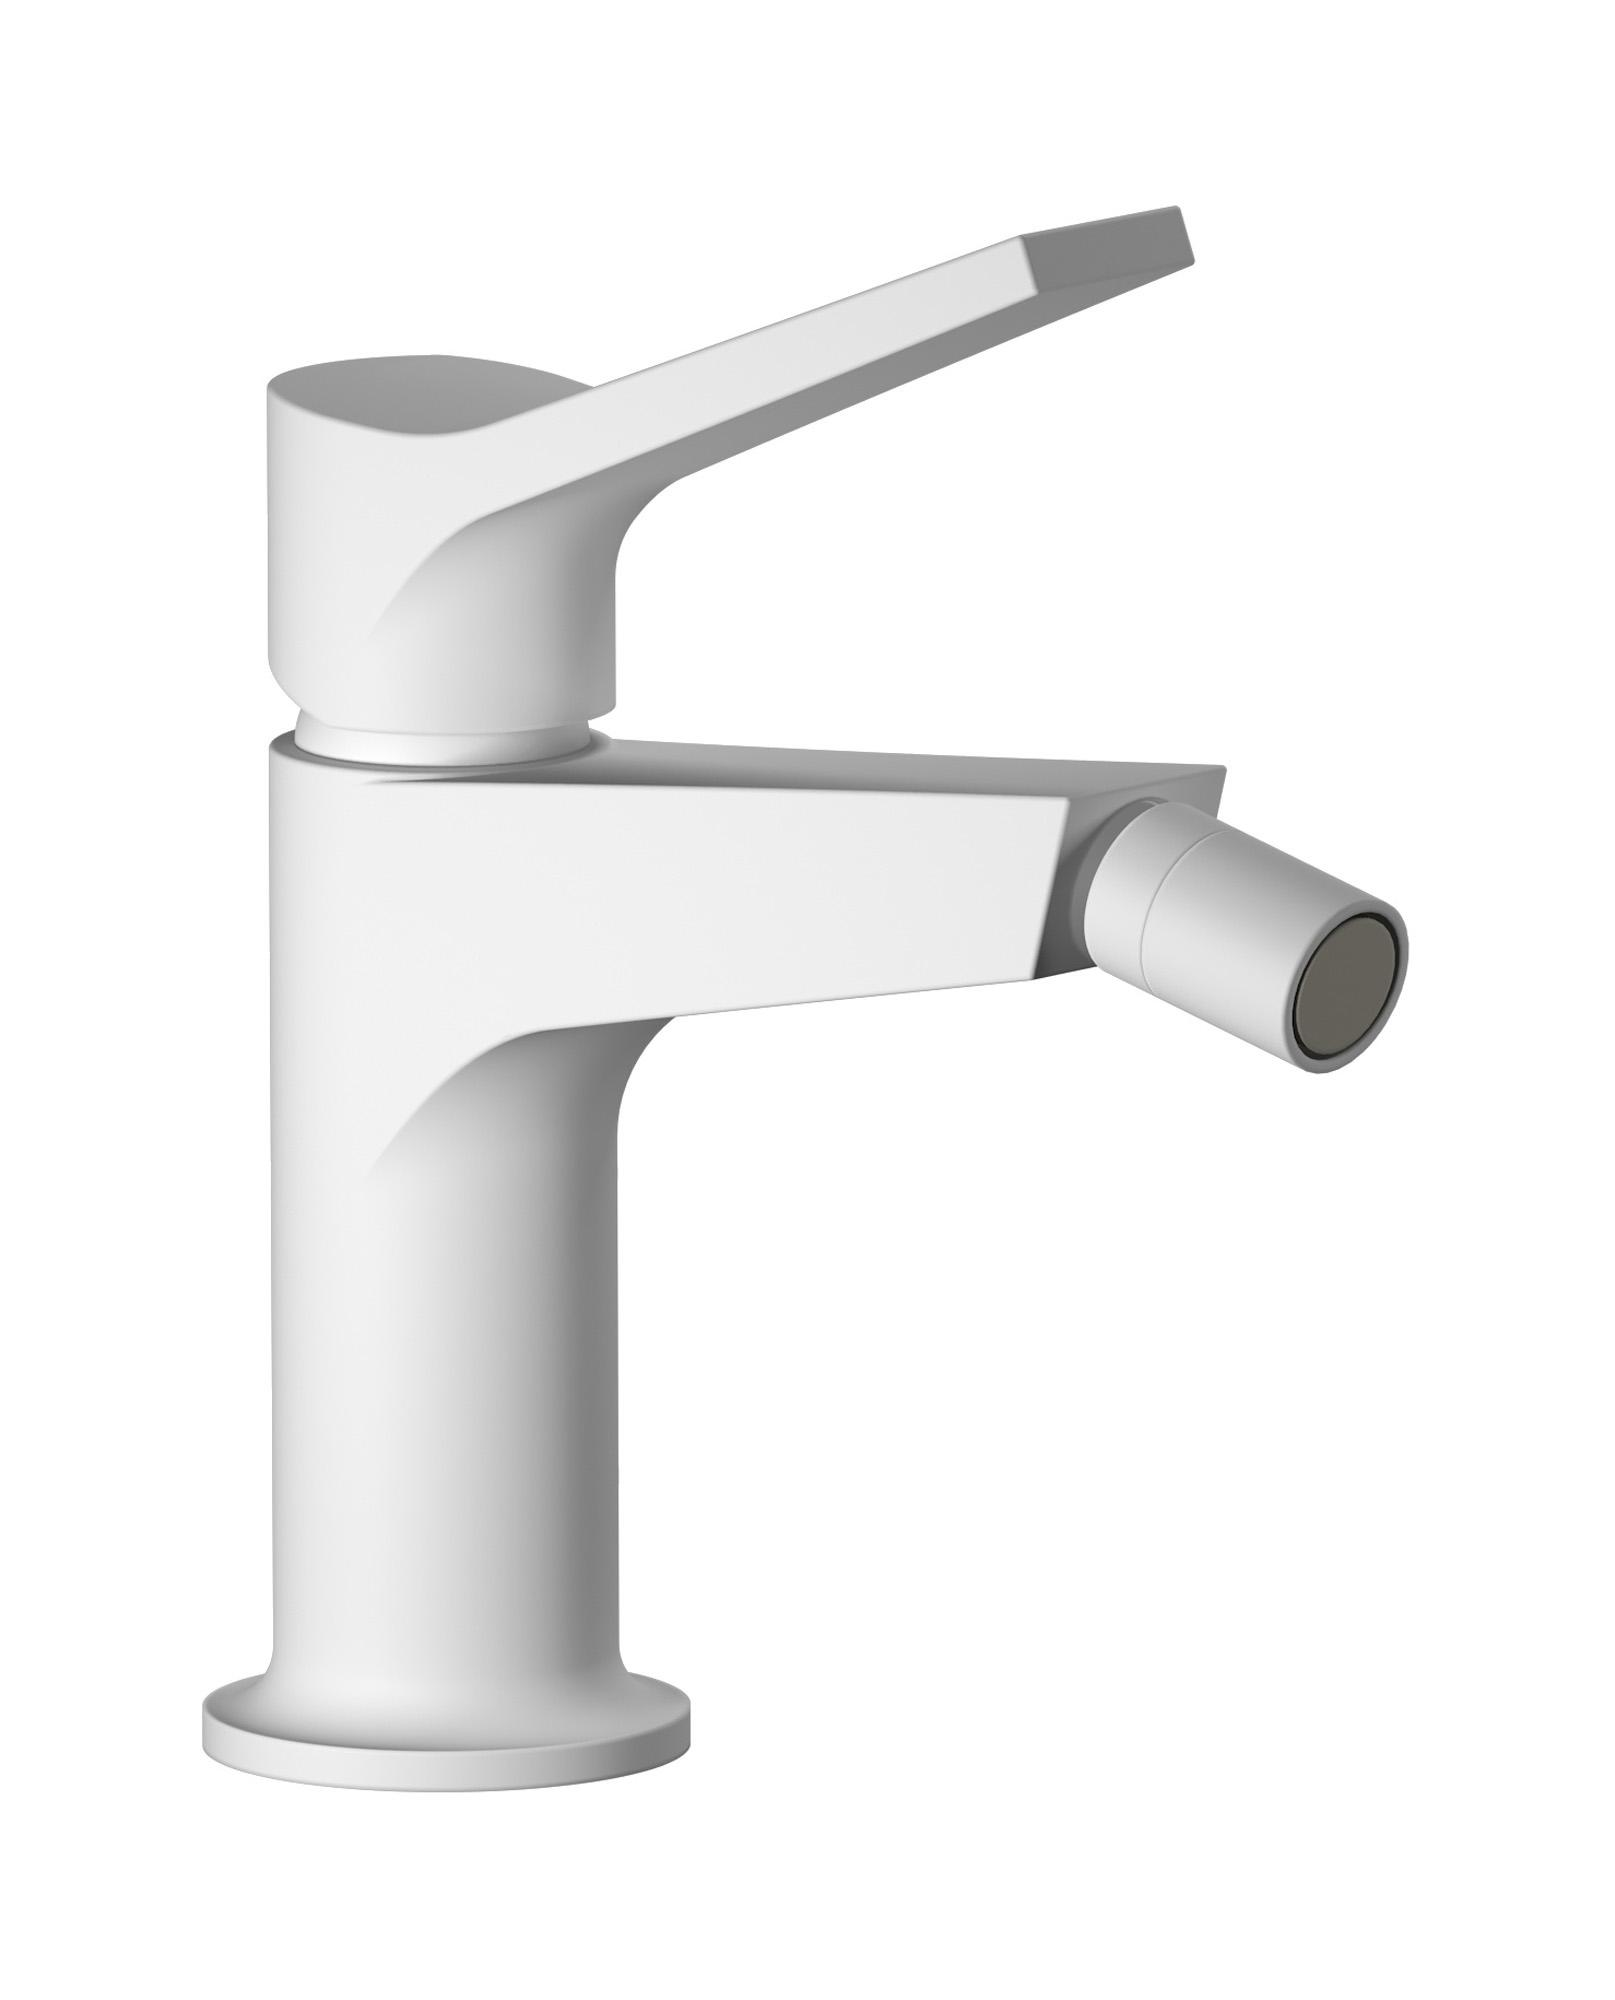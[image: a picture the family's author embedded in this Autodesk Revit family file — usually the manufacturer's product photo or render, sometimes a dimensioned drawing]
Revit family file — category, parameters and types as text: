
# Revit family: TW220
name_source: partatom
category: Apparecchi idraulici
units: mm (PartAtom-declared; Revit-internal decimal feet)

## family parameters
Basato su piano di lavoro = No
Condiviso = No
Mantieni orientamento annotazione = No
Numero OmniClass = 23.45.55.17
Punto di calcolo locali = No
Quota connettore circolare = Usa diametro
Sempre verticale = Sì
Taglio con vuoti quando caricato = No
Tipo di parte = Normale
Titolo OmniClass = Mixing Faucets

## types (12) — shared parameters
Cold water flow = 0,0 L/s
Cold water inlet = 10 mm  [stored 0.0328084 ft]
Commenti sul tipo = Bidet mixer
Connessione CW = No
Connessione HW = No
Connessione di scarico = No
Connessione di ventilazione = No
Descrizione = Monohole bidet mixer complete with drain
Hot water inlet = 10 mm  [stored 0.0328084 ft]
Produttore = IB Rubinetterie S.p.A.
URL = https://www.weareib.it
zero-valued in all types: Prospetto di default

## per-type parameters (varying)
| type | Finishes surface | Immagine tipo | Modello |
| Chrome | IB_Chrome | TW220CC.jpg | TW220CC |
| Brushed nickel | IB_Brushed nickel | TW220SS.jpg | TW220SS |
| Matt black | IB_matt black | TW220NP.jpg | TW220NP |
| Matt white | IB_matt white | TW220BO.jpg | TW220BO |
| Black chrome | IB_Black chrome | TW220CF.jpg | TW220CF |
| Brushed black chrome | IB_Brushed black chrome | TW220CS.jpg | TW220CS |
| Pale gold | IB_Pale gold | TW220II.jpg | TW220II |
| Brushed pale gold | IB_brushed pale gold | TW220IS.jpg | TW220IS |
| Rose gold | IB_Rose gold | TW220RS.jpg | TW220RS |
| Brushed rose gold | IB_Brushed rose gold | TW220SR.jpg | TW220SR |
| Gold | IB_gold | TW220OO.jpg | TW220OO |
| Brushed gold | IB_brushed gold | TW220OS.jpg | TW220OS |

note: [stored X ft] marks values corroborated as IEEE doubles in the binary element streams (Revit-internal decimal feet)
